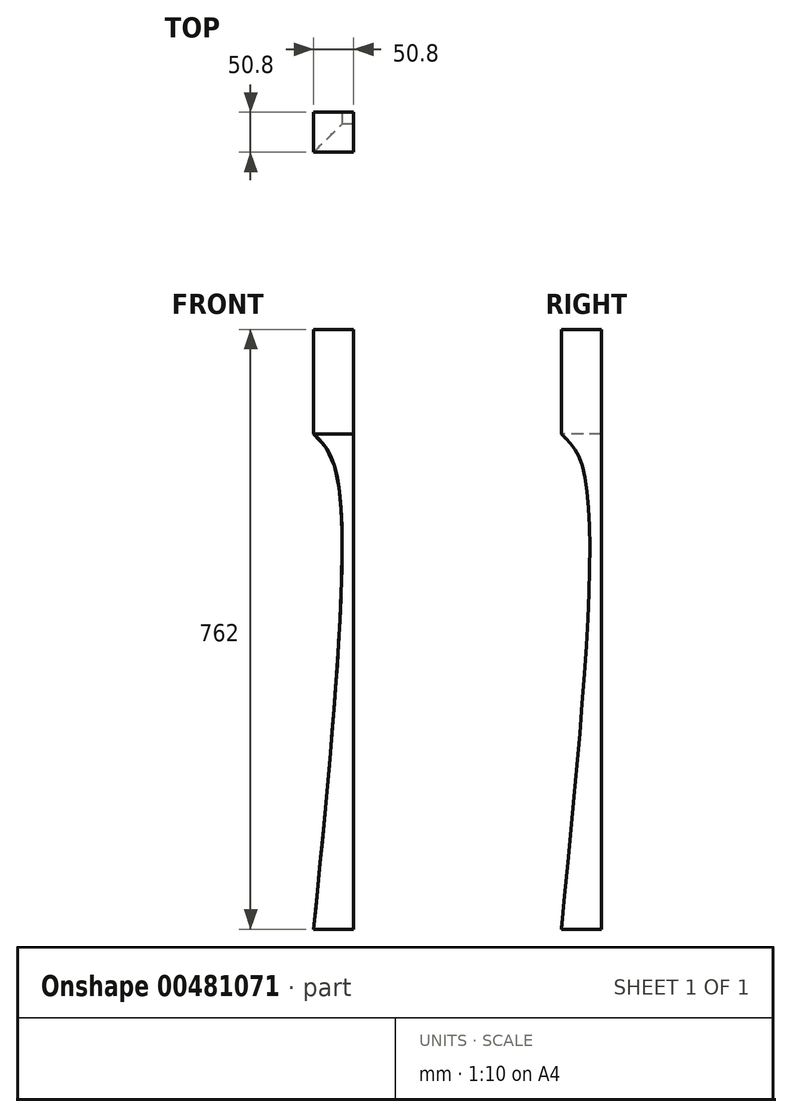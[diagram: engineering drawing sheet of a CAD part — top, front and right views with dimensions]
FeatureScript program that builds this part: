
annotation { "Feature Type Name" : "Feature", "Feature Type Description" : "" }
export const myFeature = defineFeature(function(context is Context, id is Id, definition is map)
    precondition{}
    {
        {
            var Q0;
            Q0=qCreatedBy(makeId("Front.planeOp"),FACE);
            var sketch = newSketch(context, id + "F0", { "sketchPlane" : qUnion([Q0])});
            skLineSegment(sketch, "E0.bottom", {"start": v(0, 0) * mm, "end": v(50.8, 0) * mm});
            skLineSegment(sketch, "E0.top", {"start": v(0, 762) * mm, "end": v(50.8, 762) * mm});
            skLineSegment(sketch, "E0.left", {"start": v(0, 0) * mm, "end": v(0, 762) * mm});
            skLineSegment(sketch, "E0.right", {"start": v(50.8, 0) * mm, "end": v(50.8, 762) * mm});
            skSolve(sketch);
        }
        {
            var Q0;
            Q0=makeQuery(id+"F0.imprint","IMPRINT",FACE,{"disambiguationData":[TD([[makeQuery(id+"F0.imprint","IMPRINT",EDGE,{"derivedFrom":sQuery(id+"F0.wireOp",EDGE,"E0.bottom")}),1.0]])]});
            extrude(context, id + "F1", {"entities" : qUnion([Q0]), "depth" : 50.8 * mm});
        }
        {
            var Q0;
            Q0=makeQuery(id+"F1.opExtrude","SWEPT_FACE",FACE,{"disambiguationData":[OSD([sQuery(id+"F0.wireOp",EDGE,"E0.left")])]});
            var sketch = newSketch(context, id + "F2", { "sketchPlane" : qUnion([Q0])});
            skLineSegment(sketch, "E1", {"start": v(50.8, 628.87) * mm, "end": v(50.8, 0) * mm});
            skFitSpline(sketch, "E2.MirrorCS", {"points": [v(50.8, 628.87) * mm, v(23.03, 584.58) * mm, v(50.8, 0) * mm], "startDerivative": vector(-138.73, -127.25) * mm, "endDerivative": vector(96.42, -977.5) * mm});
            skSolve(sketch);
        }
        {
            var Q0;
            Q0 = qSketchRegion(id + "F2", true);
            extrude(context, id + "F3", {"entities" : qUnion([Q0]), "operationType" : NewBodyOperationType.REMOVE, "endBound" : BoundingType.THROUGH_ALL, "oppositeDirection" : true, "depth" : 25.4 * mm});
        }
        {
            var Q0;
            Q0=makeQuery(id+"F1.opExtrude","CAP_FACE",FACE,{"disambiguationData":[OSD([sQuery(id+"F0.wireOp",EDGE,"E0.bottom"),sQuery(id+"F0.wireOp",EDGE,"E0.top"),sQuery(id+"F0.wireOp",EDGE,"E0.left"),sQuery(id+"F0.wireOp",EDGE,"E0.right")])],"isStart":false});
            var sketch = newSketch(context, id + "F4", { "sketchPlane" : qUnion([Q0])});
            skFitSpline(sketch, "E3", {"points": [v(0, 628.87) * mm, v(27.77, 584.58) * mm, v(0, 0) * mm], "startDerivative": vector(138.73, -127.25) * mm, "endDerivative": vector(-96.42, -977.5) * mm});
            skLineSegment(sketch, "E4", {"start": v(0, 628.87) * mm, "end": v(0, 0) * mm});
            skSolve(sketch);
        }
        {
            var Q0;
            Q0 = qSketchRegion(id + "F4", true);
            extrude(context, id + "F5", {"entities" : qUnion([Q0]), "operationType" : NewBodyOperationType.REMOVE, "endBound" : BoundingType.THROUGH_ALL, "oppositeDirection" : true, "depth" : 25.4 * mm});
        }
    });
